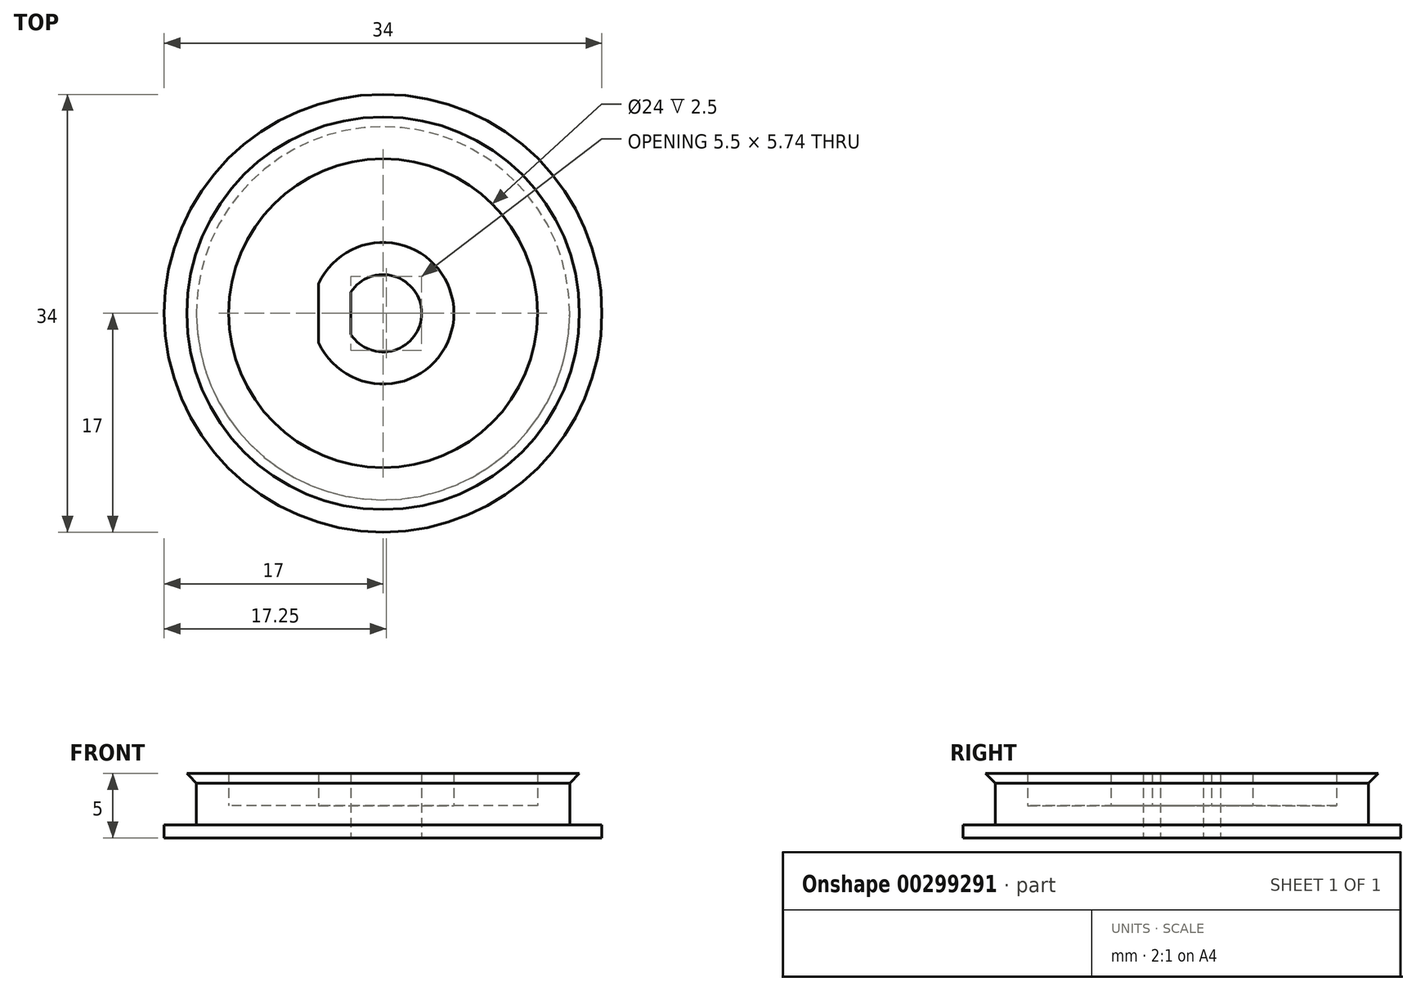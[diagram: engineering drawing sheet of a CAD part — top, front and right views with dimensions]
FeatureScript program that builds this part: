
annotation { "Feature Type Name" : "Feature", "Feature Type Description" : "" }
export const myFeature = defineFeature(function(context is Context, id is Id, definition is map)
    precondition{}
    {
        {
            var Q0;
            Q0=qCreatedBy(makeId("Top.planeOp"),FACE);
            var sketch = newSketch(context, id + "F0", { "sketchPlane" : qUnion([Q0])});
            skCircle(sketch, "E0", {"center": v(0, 0) * mm, "radius": 3 * mm});
            skCircle(sketch, "E1", {"center": v(0, 0) * mm, "radius": 14.5 * mm});
            skLineSegment(sketch, "E2", {"start": v(-2.5, 1.66) * mm, "end": v(-2.5, -1.66) * mm});
            skSolve(sketch);
        }
        {
            var Q0;
            {var subQ0=sQuery(id+"F0.wireOp",EDGE,"E2");Q0=makeQuery(id+"F0.imprint","IMPRINT",FACE,{"disambiguationData":[TD([[makeQuery(id+"F0.imprint","IMPRINT",EDGE,{"derivedFrom":subQ0}),-1.0]])]});}
            var Q1;
            Q1=makeQuery(id+"F0.imprint","IMPRINT",FACE,{"disambiguationData":[TD([[makeQuery(id+"F0.imprint","IMPRINT",EDGE,{"derivedFrom":sQuery(id+"F0.wireOp",EDGE,"E1")}),1.0]])]});
            extrude(context, id + "F1", {"entities" : qUnion([Q0, Q1]), "depth" : 5 * mm});
        }
        {
            var Q0;
            Q0=qCreatedBy(makeId("Right.planeOp"),FACE);
            var sketch = newSketch(context, id + "F2", { "sketchPlane" : qUnion([Q0])});
            skLineSegment(sketch, "E3", {"start": v(0, 21.55) * mm, "end": v(0, -14.06) * mm, "construction": true});
            skLineSegment(sketch, "E4", {"start": v(-14.5, 0) * mm, "end": v(-14.5, 5) * mm});
            skLineSegment(sketch, "E5", {"start": v(-14.5, 5) * mm, "end": v(-17, 5) * mm});
            skLineSegment(sketch, "E6", {"start": v(-17, 5) * mm, "end": v(-17, 0) * mm});
            skLineSegment(sketch, "E7", {"start": v(-17, 0) * mm, "end": v(-14.5, 0) * mm});
            skLineSegment(sketch, "E8", {"start": v(-17, 1) * mm, "end": v(-14.5, 1) * mm});
            skLineSegment(sketch, "E9", {"start": v(-15.25, 5) * mm, "end": v(-14.5, 4.25) * mm});
            skSolve(sketch);
        }
        {
            var Q0;
            {var subQ0=sQuery(id+"F2.wireOp",EDGE,"E7");Q0=makeQuery(id+"F2.imprint","IMPRINT",FACE,{"disambiguationData":[TD([[makeQuery(id+"F2.imprint","IMPRINT",EDGE,{"derivedFrom":subQ0}),1.0]])]});}
            var Q1;
            {var subQ3=sQuery(id+"F2.wireOp",EDGE,"E9");Q1=makeQuery(id+"F2.imprint","IMPRINT",FACE,{"disambiguationData":[TD([[makeQuery(id+"F2.imprint","IMPRINT",EDGE,{"derivedFrom":subQ3}),1.0]])]});}
            var Q2;
            Q2=sQuery(id+"F2.wireOp",EDGE,"E3");
            revolve(context, id + "F3", {"operationType" : NewBodyOperationType.ADD, "entities" : qUnion([Q0, Q1]), "axis" : qUnion([Q2]), "revolveType" : RevolveType.FULL, "oppositeDirection" : true});
        }
        {
            var Q0;
            Q0=makeQuery(id+"F1.opExtrude","CAP_FACE",FACE,{"disambiguationData":[OSD([sQuery(id+"F0.wireOp",EDGE,"E0"),sQuery(id+"F0.wireOp",EDGE,"E1"),sQuery(id+"F0.wireOp",EDGE,"E2")])],"isStart":false});
            shell(context, id + "F4", {"entities" : qUnion([Q0]), "thickness" : 2.5 * mm});
        }
    });
